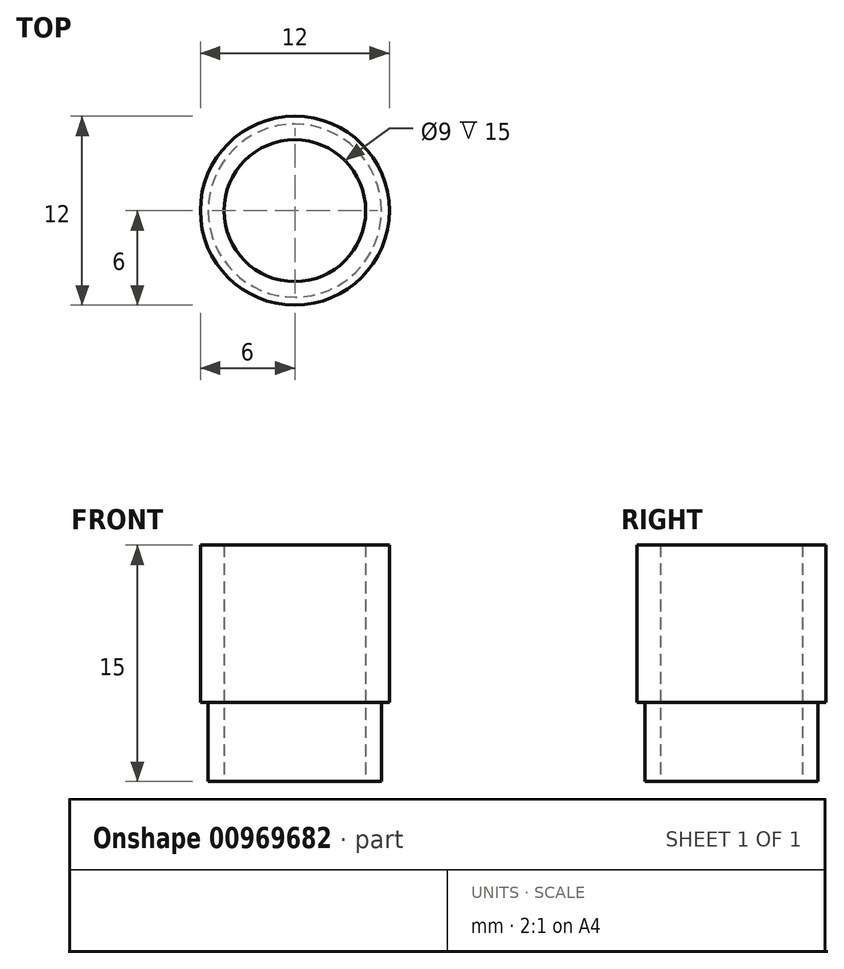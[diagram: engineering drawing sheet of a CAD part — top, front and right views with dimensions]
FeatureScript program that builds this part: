
annotation { "Feature Type Name" : "Feature", "Feature Type Description" : "" }
export const myFeature = defineFeature(function(context is Context, id is Id, definition is map)
    precondition{}
    {
        {
            var Q0;
            Q0=qCreatedBy(makeId("Top.planeOp"),FACE);
            var sketch = newSketch(context, id + "F0", { "sketchPlane" : qUnion([Q0])});
            skCircle(sketch, "E0", {"center": v(0, 0) * mm, "radius": 4.5 * mm});
            skCircle(sketch, "E1", {"center": v(0, 0) * mm, "radius": 5.5 * mm});
            skSolve(sketch);
        }
        {
            var Q0;
            Q0 = qSketchRegion(id + "F0", true);
            extrude(context, id + "F1", {"entities" : qUnion([Q0]), "depth" : 5 * mm, "offsetDistance" : 25.4 * mm});
        }
        {
            var Q0;
            Q0=makeQuery(id+"F1.opExtrude","CAP_FACE",FACE,{"disambiguationData":[OSD([sQuery(id+"F0.wireOp",EDGE,"E0"),sQuery(id+"F0.wireOp",EDGE,"E1")])],"isStart":false});
            var sketch = newSketch(context, id + "F2", { "sketchPlane" : qUnion([Q0])});
            skCircle(sketch, "E2", {"center": v(0, 0) * mm, "radius": 6 * mm});
            skSolve(sketch);
        }
        {
            var Q0;
            Q0=makeQuery(id+"F2.imprint","IMPRINT",FACE,{"disambiguationData":[TD([[makeQuery(id+"F2.imprint","IMPRINT",EDGE,{"derivedFrom":makeQuery(id+"F1.opExtrude","CAP_EDGE",EDGE,{"disambiguationData":[OSD([sQuery(id+"F0.wireOp",EDGE,"E0")])],"isStart":false})}),-1.0]])]});
            var Q1;
            Q1=makeQuery(id+"F2.imprint","IMPRINT",FACE,{"disambiguationData":[TD([[makeQuery(id+"F2.imprint","IMPRINT",EDGE,{"derivedFrom":sQuery(id+"F2.wireOp",EDGE,"E2")}),1.0]])]});
            var Q2;
            Q2=sQuery(id+"F2.wireOp",EDGE,"E2");
            extrude(context, id + "F3", {"entities" : qUnion([Q0, Q1]), "operationType" : NewBodyOperationType.ADD, "surfaceEntities" : qUnion([Q2]), "depth" : 10 * mm, "offsetDistance" : 25.4 * mm});
        }
    });
